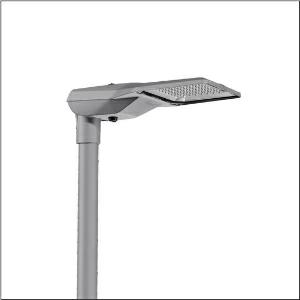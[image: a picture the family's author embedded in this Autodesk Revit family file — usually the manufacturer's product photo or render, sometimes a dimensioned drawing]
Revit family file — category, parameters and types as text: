
# Revit family: streetlight_sl_21_iq_midi___st1_0a_5xe3d51y08nb_3932
name_source: partatom
category: Lighting Fixtures
units: mm (PartAtom-declared; Revit-internal decimal feet)

## family parameters
Cut with Voids When Loaded = No
Host = Face
Light Source = No
Part Type = Normal
Room Calculation Point = No
Round Connector Dimension = Use Diameter
Shared = No

## types (1)
- --- (1 x LED, 18920 lm, 136.6 W, 3000K)
    Apparent Load = 137 VA
    CIE Flux Codes = 40 73 97 100 100
    Color Rendering = 80
    Color Temperature = 3000K
    Default Elevation = 1800 mm
    Description = Streetlight SL 21 iQ midi, mast luminaire, primary light control with lens, of PMMA, primary optical cover: cover, of toughened safety glass, transparent, light distribution: ST1.0a, light emission: direct distribution, primary light characteristic: asymmetric, installation type: post-top, side-entry, LED, High Power LED, rated luminous flux: 18.920lm, luminous efficacy: 139lm/W, light colour: 830, colour temperature: 3000K, control: pre-setting: logarithmic dimming characteristic, Street-Remote, Auto-Match, Temp-Guard, Lumen-Switch, Night-Set, Smart-Wire, Light-Fading, Desk-Remote (wireless, voltage-free reading and setting of iQ features in the workshop via application-optimized NFC function/RFID function), optimised constant luminous flux control (CLO 2.0), mains connection: 230..240V, AC, 50/60Hz, start of lifetime: 137W, end of service life: 144W, reduction: 61W, luminaire housing, of diecast aluminium, powder-coated, Siteco® metallic grey (DB 702S), corrosivity category C5 mid according to DIN EN ISO 12944, please order mast flange separately, inclination adjustable: 0°, 5°, 10°, 15°, sealing non-destructively replaceable, multi-level sealing system, length: 644mm, width: 335mm, height: 110mm, mast flange for spigot size: 42mm (side-entry): 5XC10008XM4, 60/48mm (side-entry/post-top): 5XC10108XM2, 76/60mm (side-entry/post-top): 5XC10108XM1, Smart Interface below and above, protection rating (complete): IP66, insulation class (complete): insulation class II (safety insulation), certification: CE, ENEC, ENEC+, VDE, impact resistance: IK09, permissible operating ambient temperature for outdoor applications: -40..+50°C, standard-compliant lighting for roads and squares, packaging unit: 1 piece

Light Distribution: ST1.0a
    Height = 111 mm
    Lamp = 1 x LED
    Lamp Light Flux = 18920 lm
    Lamp Power = 136.6 W
    Lamp count = 1
    Length = 644 mm
    Luminous efficacy = 139 lm/W
    Manufacturer = Siteco
    ModVariant = No
    Model = 5XE3D51Y08NB
    Number of Poles = 1
    OnlyDefault = Yes
    Power Factor = 1
    Product Name = Streetlight SL 21 iQ midi | ST1.0a
    Product group = mast luminaire | pylon top
    ProductGroupID = 6100
    Protection Class = Protection class II
    Protection Degree = IP 66
    RLX_Detail_Level = 1
    RLX_Emergency_Light_Flux = 0 lm
    RLX_Emergency_Type = 0
    RLX_Emergency_Type_DB = No
    RlxData = <blob elided: 91553 chars, md5=61aa5e2f>
    Socket = socket
    Standby Power = 0 W
    System Light Flux = 18920 lm
    System Power = 137 W
    Type Comments = factory setting: luminous flux: 100 % | dim-lin: 254 | 733 mA
    Type Image = l_1004304.jpg
    URL = http://relux.com
    VarID = @adj_082615
    Voltage = 0 V
    Weight = 0.00 kg
    Width = 336 mm

## geometry (parser evidence)
native form markers: Blend x4, Sweep x12
no freeform markers — native parametric forms only
